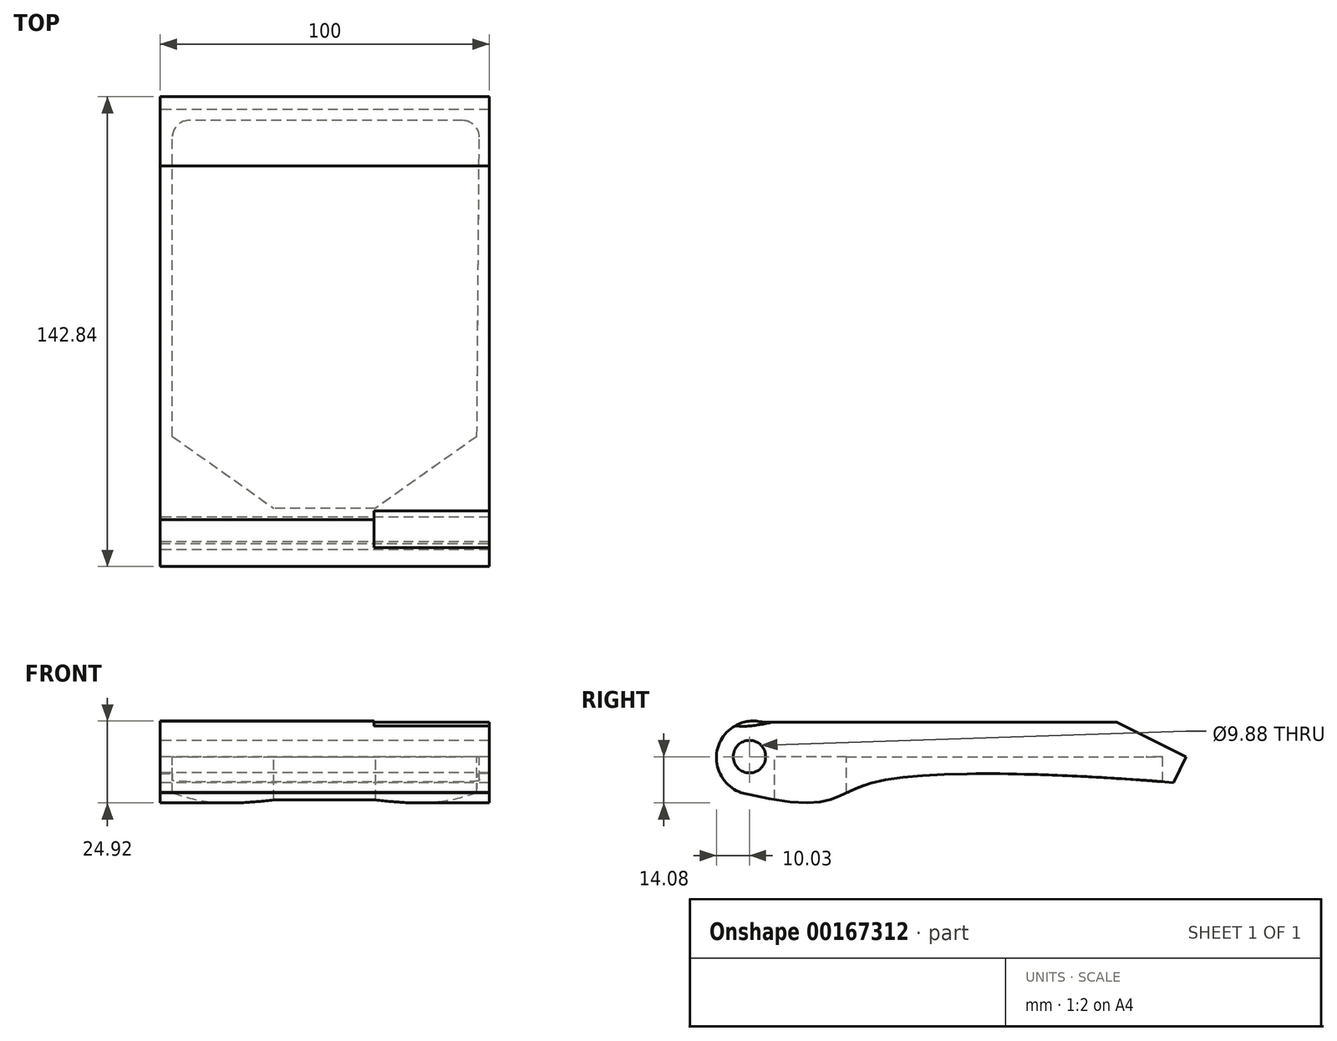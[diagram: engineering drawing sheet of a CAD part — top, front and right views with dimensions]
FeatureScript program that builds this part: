
annotation { "Feature Type Name" : "Feature", "Feature Type Description" : "" }
export const myFeature = defineFeature(function(context is Context, id is Id, definition is map)
    precondition{}
    {
        {
            var Q0;
            Q0=qCreatedBy(makeId("Right.planeOp"),FACE);
            var sketch = newSketch(context, id + "F0", { "sketchPlane" : qUnion([Q0])});
            skCircle(sketch, "E0", {"center": v(0, 0) * mm, "radius": 4.94 * mm});
            skArc(sketch, "E1", {"start": v(-3.03, -10.82) * mm, "mid": v(-2.75, -10.9) * mm, "end": v(-2.47, -10.96) * mm});
            skLineSegment(sketch, "E2", {"start": v(4.2, 10.42) * mm, "end": v(111.72, 10.42) * mm});
            skLineSegment(sketch, "E3", {"start": v(111.72, 10.42) * mm, "end": v(132.81, 0) * mm});
            skLineSegment(sketch, "E4", {"start": v(132.81, 0) * mm, "end": v(128.91, -7.9) * mm});
            skFitSpline(sketch, "E5", {"points": [v(-3.03, -10.82) * mm, v(37.6, -7.9) * mm, v(128.91, -7.9) * mm], "startDerivative": vector(217.12, -55.15) * mm, "endDerivative": vector(113.82, -9.64) * mm});
            skArc(sketch, "E6", {"start": v(4.2, 10.42) * mm, "mid": v(-9.53, 2.97) * mm, "end": v(-2.47, -10.96) * mm});
            skSolve(sketch);
        }
        {
            var Q0;
            Q0 = qSketchRegion(id + "F0", true);
            extrude(context, id + "F1", {"entities" : qUnion([Q0]), "endBound" : BoundingType.SYMMETRIC, "depth" : 100 * mm});
        }
        {
            var Q0;
            Q0=makeQuery(id+"F1.opExtrude","CAP_FACE",FACE,{"disambiguationData":[OSD([sQuery(id+"F0.wireOp",EDGE,"E0"),sQuery(id+"F0.wireOp",EDGE,"E2"),sQuery(id+"F0.wireOp",EDGE,"E3"),sQuery(id+"F0.wireOp",EDGE,"E4"),sQuery(id+"F0.wireOp",EDGE,"E5"),sQuery(id+"F0.wireOp",EDGE,"E6")])],"isStart":false});
            var sketch = newSketch(context, id + "F2", { "sketchPlane" : qUnion([Q0])});
            skLineSegment(sketch, "E7.0", {"start": v(4.2, 10.42) * mm, "end": v(12.69, 10.42) * mm});
            skArc(sketch, "E7.1", {"start": v(4.2, 10.42) * mm, "mid": v(-9.53, 2.97) * mm, "end": v(-2.47, -10.96) * mm});
            skFitSpline(sketch, "E7.2", {"points": [v(-3.03, -10.82) * mm, v(25.95, -18.18) * mm, v(23.43, -0.84) * mm, v(106.17, -5.97) * mm, v(128.91, -7.9) * mm]});
            skCircle(sketch, "E7.3", {"center": v(0, 0) * mm, "radius": 4.94 * mm});
            skFitSpline(sketch, "E8", {"points": [v(2.98, -12.24) * mm, v(12.69, 10.42) * mm, v(-4.33, 9.4) * mm, v(-23.86, 28.04) * mm], "startDerivative": vector(53.22, 88.44) * mm, "endDerivative": vector(-46.42, 71.92) * mm});
            skPoint(sketch, "E9.orphan", {"position": v(111.72, 10.42) * mm});
            skPoint(sketch, "E10.orphan", {"position": v(128.91, -7.9) * mm});
            skSolve(sketch);
        }
        {
            var Q0;
            Q0 = qSketchRegion(id + "F2", true);
            extrude(context, id + "F3", {"entities" : qUnion([Q0]), "operationType" : NewBodyOperationType.REMOVE, "oppositeDirection" : true, "depth" : 35 * mm});
        }
        {
            var Q0;
            Q0=qCreatedBy(makeId("Top.planeOp"),FACE);
            var sketch = newSketch(context, id + "F4", { "sketchPlane" : qUnion([Q0])});
            skLineSegment(sketch, "E11.bottom", {"start": v(-15.51, 7.68) * mm, "end": v(15.51, 7.68) * mm});
            skLineSegment(sketch, "E11.top", {"start": v(-41.3, 125.6) * mm, "end": v(42, 125.6) * mm});
            skLineSegment(sketch, "E11.left", {"start": v(-46.3, 29.53) * mm, "end": v(-46.3, 120.6) * mm});
            skLineSegment(sketch, "E12", {"start": v(-46.3, 29.53) * mm, "end": v(-15.51, 7.68) * mm});
            skLineSegment(sketch, "E13.MirrorCS", {"start": v(46.3, 29.53) * mm, "end": v(15.51, 7.68) * mm});
            skLineSegment(sketch, "E14", {"start": v(46.3, 29.53) * mm, "end": v(47, 120.56) * mm});
            skPoint(sketch, "E15.visualSharp", {"position": v(-46.3, 125.6) * mm});
            skArc(sketch, "E15.filletArc", {"start": v(-41.3, 125.6) * mm, "mid": v(-44.83, 124.13) * mm, "end": v(-46.3, 120.6) * mm});
            skPoint(sketch, "E16.visualSharp", {"position": v(47.04, 125.6) * mm});
            skArc(sketch, "E16.filletArc", {"start": v(47, 120.56) * mm, "mid": v(45.55, 124.12) * mm, "end": v(42, 125.6) * mm});
            skSolve(sketch);
        }
        {
            var Q0;
            Q0 = qSketchRegion(id + "F4", true);
            extrude(context, id + "F5", {"entities" : qUnion([Q0]), "operationType" : NewBodyOperationType.REMOVE, "oppositeDirection" : true, "depth" : 25 * mm});
        }
    });
